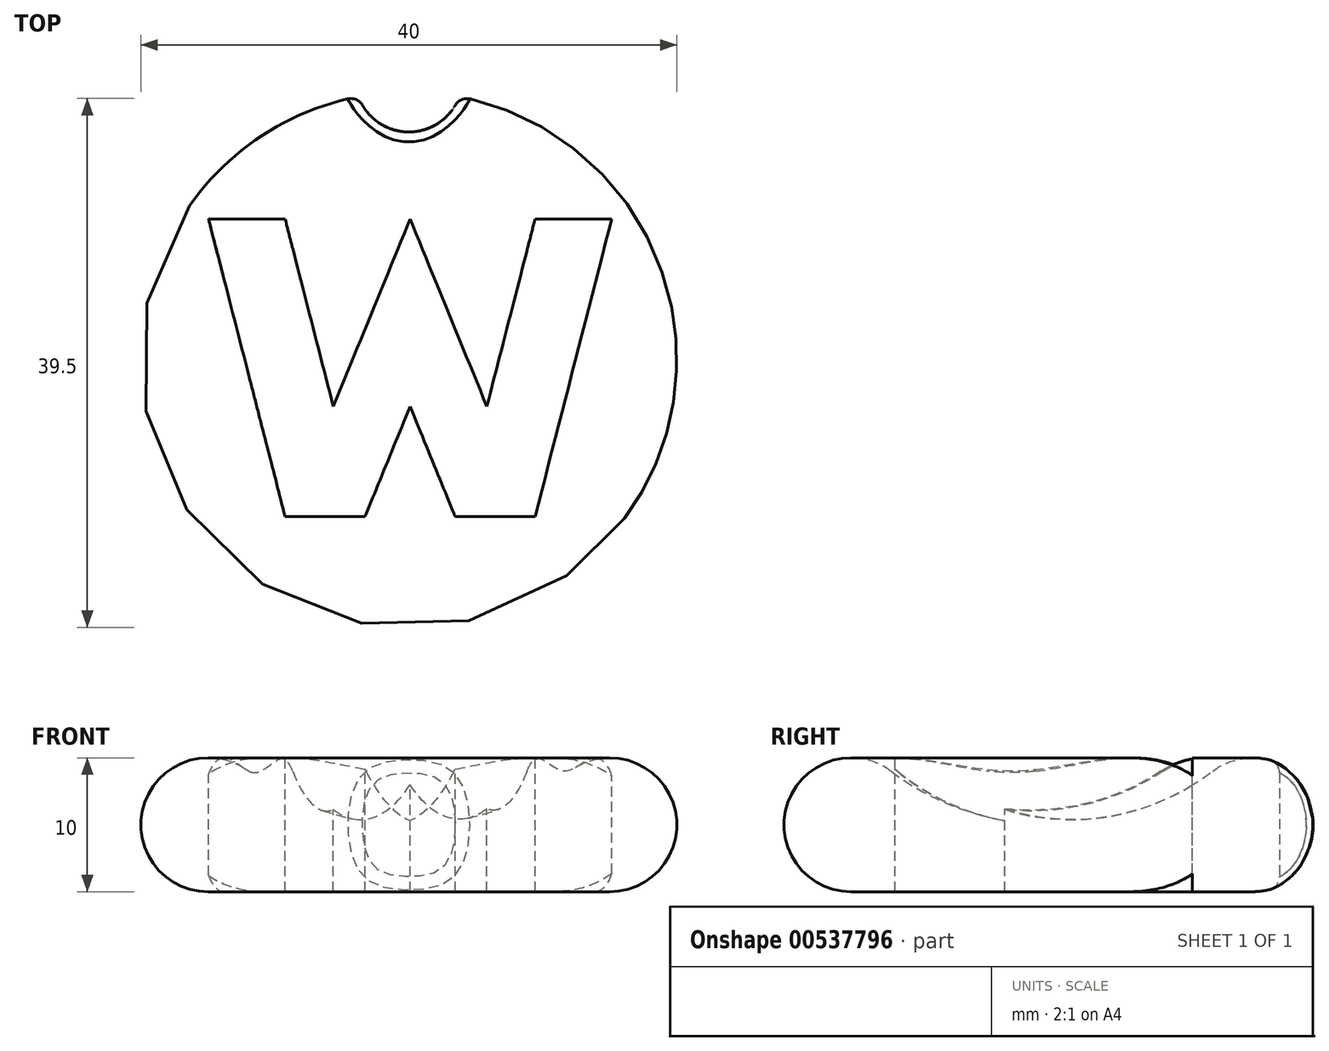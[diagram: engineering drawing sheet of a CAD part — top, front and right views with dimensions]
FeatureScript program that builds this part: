
annotation { "Feature Type Name" : "Feature", "Feature Type Description" : "" }
export const myFeature = defineFeature(function(context is Context, id is Id, definition is map)
    precondition{}
    {
        {
            var Q0;
            Q0=qCreatedBy(makeId("Front.planeOp"),FACE);
            var sketch = newSketch(context, id + "F0", { "sketchPlane" : qUnion([Q0])});
            skArc(sketch, "E0", {"start": v(-12, 9) * mm, "mid": v(-6.32, 6.03) * mm, "end": v(0, 5) * mm});
            skArc(sketch, "E1", {"start": v(-12, 9) * mm, "mid": v(-19.74, 6.58) * mm, "end": v(-15, 0) * mm});
            skLineSegment(sketch, "E2", {"start": v(0, 0) * mm, "end": v(0, 5) * mm});
            skLineSegment(sketch, "E3", {"start": v(-15, 0) * mm, "end": v(0, 0) * mm});
            skSolve(sketch);
        }
        {
            var Q0;
            Q0=makeQuery(id+"F0.imprint","IMPRINT",FACE,{"disambiguationData":[TD([[makeQuery(id+"F0.imprint","IMPRINT",EDGE,{"derivedFrom":sQuery(id+"F0.wireOp",EDGE,"E0")}),-1.0]])]});
            var Q1;
            Q1=sQuery(id+"F0.wireOp",EDGE,"E2");
            revolve(context, id + "F1", {"entities" : qUnion([Q0]), "axis" : qUnion([Q1]), "revolveType" : RevolveType.FULL});
        }
        {
            var Q0;
            Q0=qCreatedBy(makeId("Top.planeOp"),FACE);
            var sketch = newSketch(context, id + "F2", { "sketchPlane" : qUnion([Q0])});
            skCircle(sketch, "E4", {"center": v(0, 21) * mm, "radius": 4 * mm});
            skSolve(sketch);
        }
        {
            var Q0;
            Q0=makeQuery(id+"F2.imprint","IMPRINT",FACE,{"disambiguationData":[TD([[makeQuery(id+"F2.imprint","IMPRINT",EDGE,{"derivedFrom":sQuery(id+"F2.wireOp",EDGE,"E4")}),1.0]])]});
            extrude(context, id + "F3", {"entities" : qUnion([Q0]), "operationType" : NewBodyOperationType.REMOVE, "depth" : 11.66 * mm, "offsetDistance" : 25.4 * mm});
        }
        {
            var Q0;
            Q0=makeQuery(id+"F3.boolean.opBoolean","INTERSECT",EDGE,{"derivedFrom":[makeQuery(id+"F1.opRevolve","SWEPT_FACE",FACE,{"disambiguationData":[OSD([sQuery(id+"F0.wireOp",EDGE,"E1")])]}),makeQuery(id+"F3.opExtrude","SWEPT_FACE",FACE,{"disambiguationData":[OSD([sQuery(id+"F2.wireOp",EDGE,"E4")])]})]});
            fillet(context, id + "F4", {"entities" : qUnion([Q0]), "radius" : 1 * mm, "tangentPropagation" : true, "allowEdgeOverflow" : false});
        }
        {
            var Q0;
            Q0=qCreatedBy(makeId("Top.planeOp"),FACE);
            cPlane(context, id + "F5", {"entities" : qUnion([Q0]), "cplaneType" : CPlaneType.OFFSET, "offset" : 25.4 * mm, "width" : 152.4 * mm, "height" : 152.4 * mm});
        }
        {
            var Q0;
            Q0=qCreatedBy(id+"F5.planeOp",FACE);
            var sketch = newSketch(context, id + "F6", { "sketchPlane" : qUnion([Q0])});
            skLineSegment(sketch, "E5", {"start": v(-14.96, 10.5) * mm, "end": v(-9.24, -11.72) * mm});
            skLineSegment(sketch, "E6", {"start": v(-9.24, -11.72) * mm, "end": v(-3.27, -11.72) * mm});
            skLineSegment(sketch, "E7", {"start": v(-3.27, -11.72) * mm, "end": v(0.1, -3.5) * mm});
            skLineSegment(sketch, "E8", {"start": v(-14.96, 10.5) * mm, "end": v(-9.24, 10.5) * mm});
            skLineSegment(sketch, "E9", {"start": v(-9.24, 10.5) * mm, "end": v(-5.64, -3.5) * mm});
            skLineSegment(sketch, "E10", {"start": v(-5.64, -3.5) * mm, "end": v(0.1, 10.5) * mm});
            skLineSegment(sketch, "E11", {"start": v(0.1, -3.5) * mm, "end": v(0.1, -3.5) * mm});
            skLineSegment(sketch, "E12", {"start": v(0.1, 10.5) * mm, "end": v(0.1, 10.5) * mm});
            skLineSegment(sketch, "E13.MirrorCS", {"start": v(5.82, -3.5) * mm, "end": v(0.1, 10.5) * mm});
            skLineSegment(sketch, "E14.MirrorCS", {"start": v(9.42, 10.5) * mm, "end": v(5.82, -3.5) * mm});
            skLineSegment(sketch, "E15.MirrorCS", {"start": v(15.14, 10.5) * mm, "end": v(9.42, 10.5) * mm});
            skLineSegment(sketch, "E16.MirrorCS", {"start": v(15.14, 10.5) * mm, "end": v(9.42, -11.72) * mm});
            skLineSegment(sketch, "E17.MirrorCS", {"start": v(9.42, -11.72) * mm, "end": v(3.45, -11.72) * mm});
            skLineSegment(sketch, "E18.MirrorCS", {"start": v(3.45, -11.72) * mm, "end": v(0.1, -3.5) * mm});
            skSolve(sketch);
        }
        {
            var Q0;
            Q0=makeQuery(id+"F6.imprint","IMPRINT",FACE,{"disambiguationData":[TD([[makeQuery(id+"F6.imprint","IMPRINT",EDGE,{"derivedFrom":sQuery(id+"F6.wireOp",EDGE,"E5")}),1.0]])]});
            extrude(context, id + "F7", {"entities" : qUnion([Q0]), "operationType" : NewBodyOperationType.REMOVE, "oppositeDirection" : true, "depth" : 25.4 * mm, "offsetDistance" : 25.4 * mm});
        }
    });
